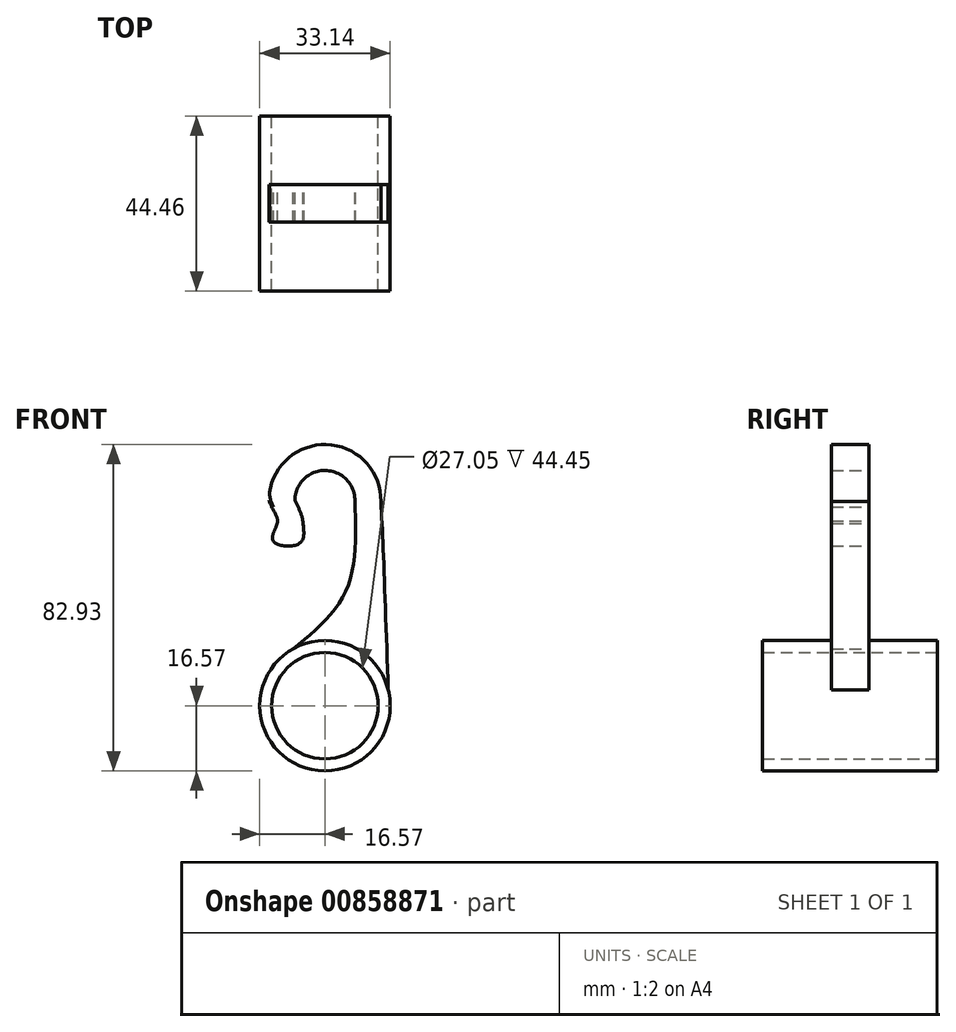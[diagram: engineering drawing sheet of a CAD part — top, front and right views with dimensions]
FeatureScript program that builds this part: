
annotation { "Feature Type Name" : "Feature", "Feature Type Description" : "" }
export const myFeature = defineFeature(function(context is Context, id is Id, definition is map)
    precondition{}
    {
        {
            var Q0;
            Q0=qCreatedBy(makeId("Front.planeOp"),FACE);
            var sketch = newSketch(context, id + "F0", { "sketchPlane" : qUnion([Q0])});
            skCircle(sketch, "E0", {"center": v(0, 0) * mm, "radius": 13.53 * mm});
            skArc(sketch, "E1", {"start": v(-8.15, 14.43) * mm, "mid": v(-6.56, -15.22) * mm, "end": v(16.09, 4) * mm});
            skArc(sketch, "E2", {"start": v(7.62, 52.06) * mm, "mid": v(0.04, 59.75) * mm, "end": v(-7.62, 52.13) * mm});
            skArc(sketch, "E3", {"start": v(14.22, 51.89) * mm, "mid": v(1.7, 66.26) * mm, "end": v(-13.88, 55.26) * mm});
            skFitSpline(sketch, "E4", {"points": [v(7.62, 52.06) * mm, v(5.34, 29.24) * mm, v(-8.15, 14.43) * mm], "startDerivative": vector(1.67, -47.64) * mm, "endDerivative": vector(-33.62, -27.38) * mm});
            skFitSpline(sketch, "E5", {"points": [v(14.22, 51.89) * mm, v(14.87, 38) * mm, v(16.09, 4) * mm], "startDerivative": vector(1.57, -31.7) * mm, "endDerivative": vector(2.13, -61.87) * mm});
            skFitSpline(sketch, "E6", {"points": [v(-7.62, 52.13) * mm, v(-5.57, 46.25) * mm, v(-7.62, 38.51) * mm], "startDerivative": vector(6.31, -12.08) * mm, "endDerivative": vector(-6.06, -15.1) * mm});
            skFitSpline(sketch, "E7", {"points": [v(-14.22, 52.13) * mm, v(-12.02, 46.9) * mm, v(-13.15, 41.82) * mm, v(-6.55, 41.18) * mm, v(-5.57, 46.25) * mm], "startDerivative": vector(14.86, -19.94) * mm, "endDerivative": vector(-3.33, 25.82) * mm});
            skFitSpline(sketch, "E8", {"points": [v(-14.22, 52.13) * mm, v(-12.98, 49.46) * mm, v(-12.02, 46.9) * mm, v(-13.35, 42.72) * mm], "startDerivative": vector(3.75, -8.68) * mm, "endDerivative": vector(-5.52, -11.61) * mm});
            skArc(sketch, "E9.filletArc", {"start": v(-13.88, 55.26) * mm, "mid": v(-13.94, 52.78) * mm, "end": v(-13.04, 50.46) * mm});
            skCircle(sketch, "E10", {"center": v(0, 0) * mm, "radius": 16.57 * mm});
            skSolve(sketch);
        }
        {
            var Q0;
            Q0=makeQuery(id+"F0.imprint","IMPRINT",FACE,{"disambiguationData":[TD([[makeQuery(id+"F0.imprint","IMPRINT",EDGE,{"derivedFrom":sQuery(id+"F0.wireOp",EDGE,"E0")}),-1.0]])]});
            extrude(context, id + "F1", {"entities" : qUnion([Q0]), "endBound" : BoundingType.SYMMETRIC, "depth" : 44.45 * mm, "offsetDistance" : 25.4 * mm});
        }
        {
            var Q0;
            Q0 = qSketchRegion(id + "F0", true);
            extrude(context, id + "F2", {"entities" : qUnion([Q0]), "operationType" : NewBodyOperationType.ADD, "endBound" : BoundingType.SYMMETRIC, "depth" : 9.52 * mm, "offsetDistance" : 25.4 * mm});
        }
    });
